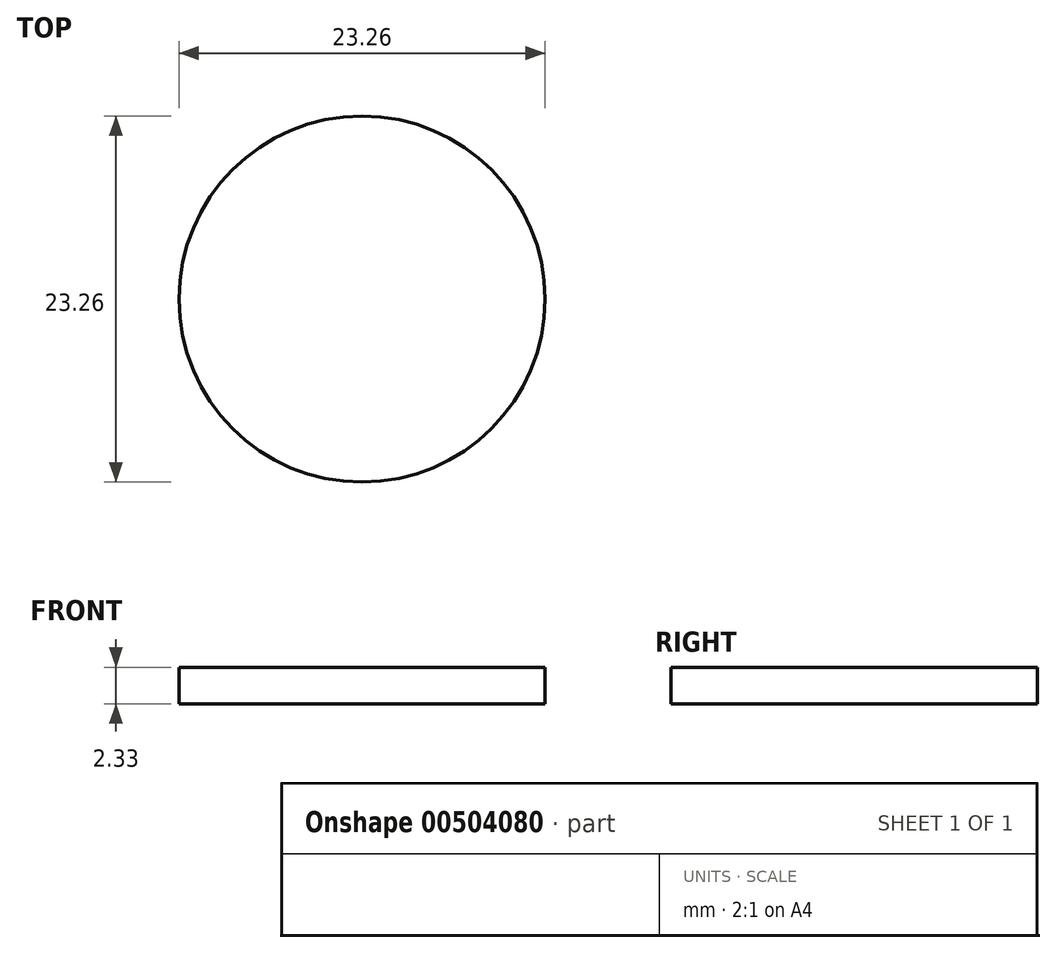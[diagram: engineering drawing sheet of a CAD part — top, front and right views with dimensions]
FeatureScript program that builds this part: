
annotation { "Feature Type Name" : "Feature", "Feature Type Description" : "" }
export const myFeature = defineFeature(function(context is Context, id is Id, definition is map)
    precondition{}
    {
        {
            var Q0;
            Q0=qCreatedBy(makeId("Top.planeOp"),FACE);
            var sketch = newSketch(context, id + "F0", { "sketchPlane" : qUnion([Q0])});
            skCircle(sketch, "E0", {"center": v(0, 0) * mm, "radius": 11.62 * mm});
            skSolve(sketch);
        }
        {
            var Q0;
            Q0 = qSketchRegion(id + "F0", true);
            extrude(context, id + "F1", {"entities" : qUnion([Q0]), "flatOperationType" : FlatOperationType.REMOVE, "offsetDistance" : 25 * mm, "depth" : 2.33 * mm, "domain" : OperationDomain.MODEL});
        }
    });
